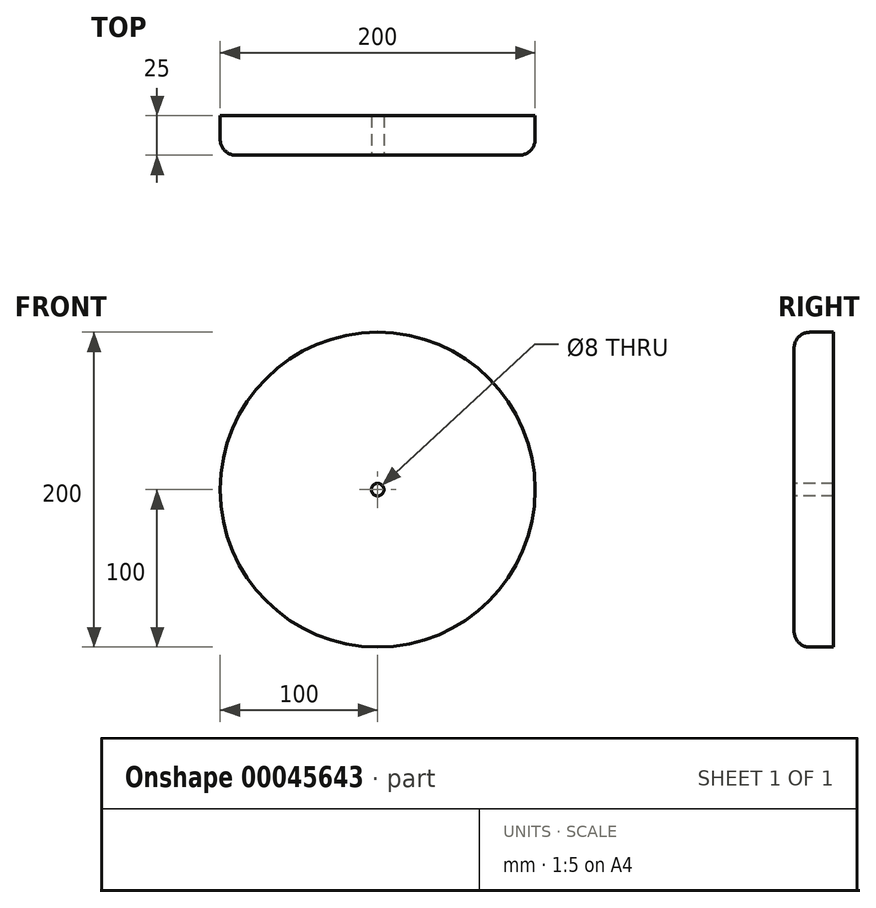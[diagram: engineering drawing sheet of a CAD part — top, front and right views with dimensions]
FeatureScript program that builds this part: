
annotation { "Feature Type Name" : "Feature", "Feature Type Description" : "" }
export const myFeature = defineFeature(function(context is Context, id is Id, definition is map)
    precondition{}
    {
        {
            var Q0;
            Q0=qCreatedBy(makeId("Front.planeOp"),FACE);
            var sketch = newSketch(context, id + "F0", { "sketchPlane" : qUnion([Q0])});
            skCircle(sketch, "E0", {"center": v(0, 0) * mm, "radius": 100 * mm});
            skSolve(sketch);
        }
        {
            var Q0;
            Q0=makeQuery(id+"F0.imprint","IMPRINT",FACE,{"disambiguationData":[TD([[makeQuery(id+"F0.imprint","IMPRINT",EDGE,{"derivedFrom":sQuery(id+"F0.wireOp",EDGE,"E0")}),1.0]])]});
            extrude(context, id + "F1", {"entities" : qUnion([Q0]), "depth" : 25 * mm});
        }
        {
            var Q0;
            Q0=makeQuery(id+"F1.opExtrude","CAP_EDGE",EDGE,{"disambiguationData":[OSD([sQuery(id+"F0.wireOp",EDGE,"E0")])],"isStart":false});
            fillet(context, id + "F2", {"entities" : qUnion([Q0]), "radius" : 10 * mm, "tangentPropagation" : true, "allowEdgeOverflow" : false});
        }
        {
            var Q0;
            Q0=makeQuery(id+"F1.opExtrude","CAP_FACE",FACE,{"disambiguationData":[OSD([sQuery(id+"F0.wireOp",EDGE,"E0")])],"isStart":false});
            var sketch = newSketch(context, id + "F3", { "sketchPlane" : qUnion([Q0])});
            skCircle(sketch, "E1", {"center": v(0, 0) * mm, "radius": 4 * mm});
            skSolve(sketch);
        }
        {
            var Q0;
            Q0=makeQuery(id+"F3.imprint","IMPRINT",FACE,{"disambiguationData":[TD([[makeQuery(id+"F3.imprint","IMPRINT",EDGE,{"derivedFrom":sQuery(id+"F3.wireOp",EDGE,"E1")}),1.0]])]});
            extrude(context, id + "F4", {"entities" : qUnion([Q0]), "operationType" : NewBodyOperationType.REMOVE, "oppositeDirection" : true, "depth" : 25 * mm});
        }
    });
